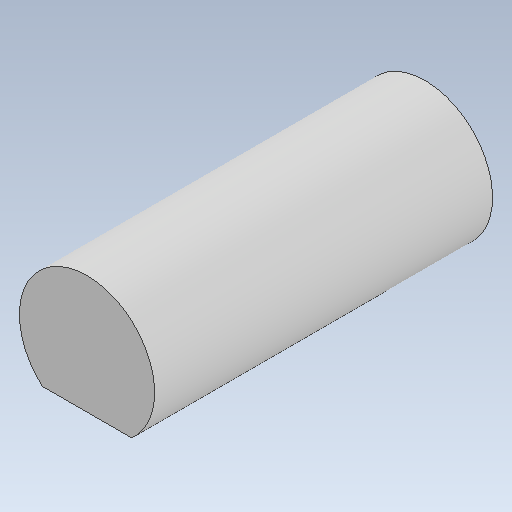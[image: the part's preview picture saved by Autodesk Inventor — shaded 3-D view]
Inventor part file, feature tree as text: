
AUTODESK INVENTOR PART (.ipt)
format: ipt  version: 2021 (Build 250183000, 183)  size: 103,936 bytes
history: native  units: mm
features: extrude x2, sketch x2
ambient origin geometry x8: Origin, YZ Plane, XZ Plane, XY Plane, X Axis, Y Axis, Z Axis, Center Point
bodies: Solid1 (feature_tree)
feature tree (4):
  extrude  "Extrusion1"  Depth=4.0mm
  extrude  "Extrusion2"  Depth=20.0mm TaperAngle=0.0deg
  sketch  "Sketch1"  dims[d3=4.0mm d4=22.931881mm]
  sketch  "Sketch2"  dims[d5=14.447836mm d6=20.0mm d7=0.0mm d8=5.0mm d9=0.0mm]
